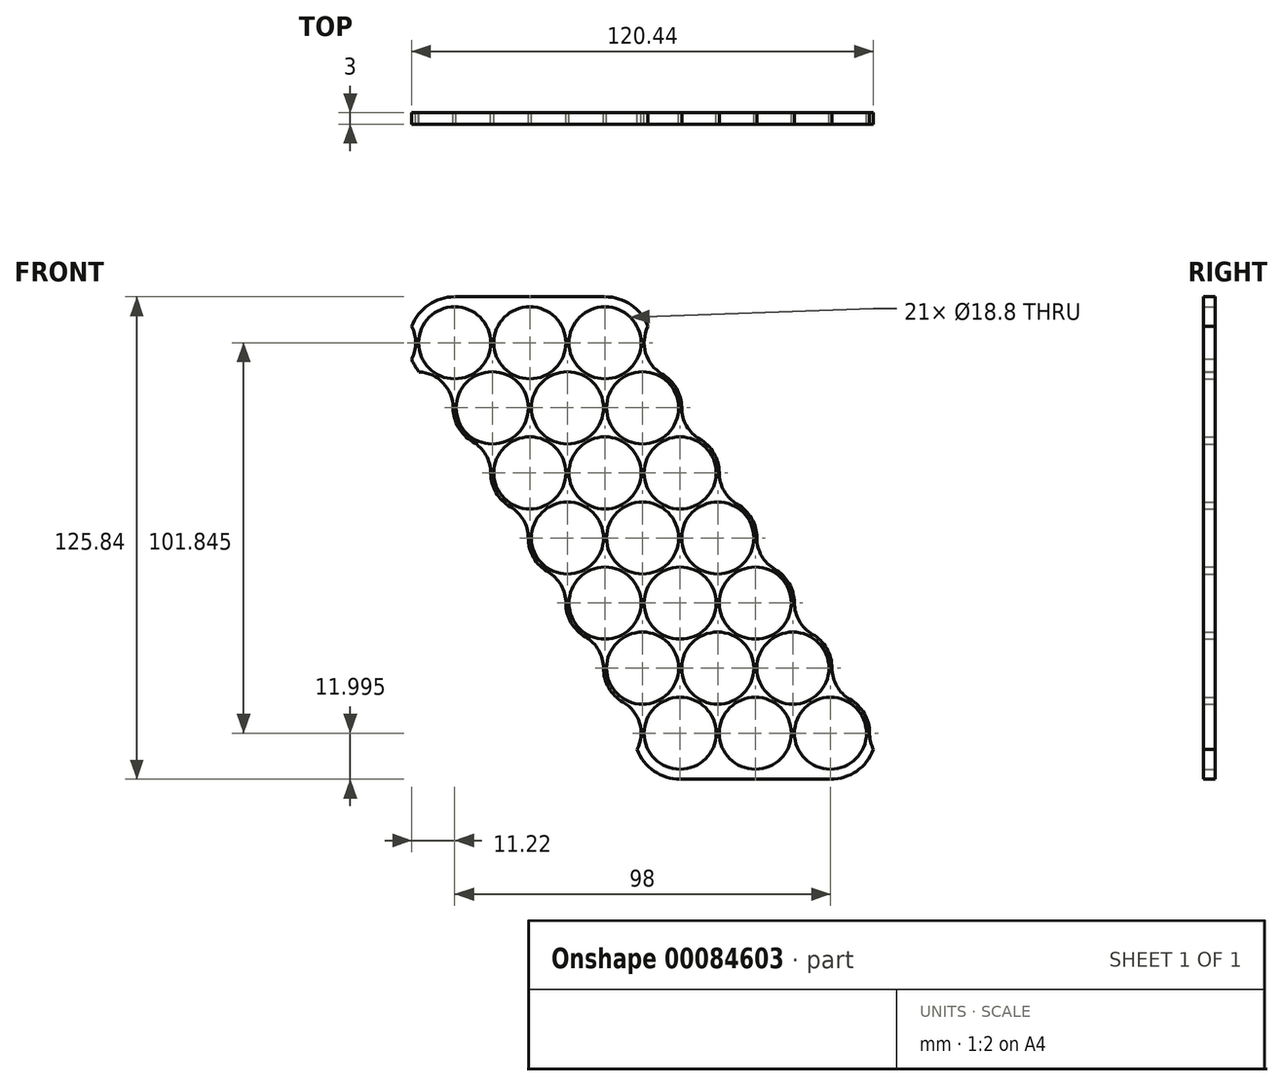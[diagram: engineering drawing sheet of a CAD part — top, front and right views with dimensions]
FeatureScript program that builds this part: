
annotation { "Feature Type Name" : "Feature", "Feature Type Description" : "" }
export const myFeature = defineFeature(function(context is Context, id is Id, definition is map)
    precondition{}
    {
        {
            var Q0;
            Q0=qCreatedBy(makeId("Front.planeOp"),FACE);
            var sketch = newSketch(context, id + "F0", { "sketchPlane" : qUnion([Q0]) });
            skLineSegment(sketch, "E0", {"start": v(0, 0) * mm, "end": v(43.4, -75.16) * mm, "construction": true});
            skCircle(sketch, "E1", {"center": v(0, 0) * mm, "radius": 9.4 * mm});
            skCircle(sketch, "E2.1.0.0", {"center": v(19.6, 0) * mm, "radius": 9.4 * mm});
            skCircle(sketch, "E2.2.0.0", {"center": v(39.2, 0) * mm, "radius": 9.4 * mm});
            skLineSegment(sketch, "E2.direction1", {"start": v(0, 0) * mm, "end": v(19.6, 0) * mm, "construction": true});
            skCircle(sketch, "E3.1.0.0", {"center": v(9.8, -16.97) * mm, "radius": 9.4 * mm});
            skCircle(sketch, "E3.2.0.0", {"center": v(19.6, -33.95) * mm, "radius": 9.4 * mm});
            skCircle(sketch, "E3.3.0.0", {"center": v(29.4, -50.92) * mm, "radius": 9.4 * mm});
            skCircle(sketch, "E3.4.0.0", {"center": v(39.2, -67.9) * mm, "radius": 9.4 * mm});
            skCircle(sketch, "E3.5.0.0", {"center": v(49, -84.87) * mm, "radius": 9.4 * mm});
            skCircle(sketch, "E3.6.0.0", {"center": v(58.8, -101.84) * mm, "radius": 9.4 * mm});
            skLineSegment(sketch, "E3.direction1", {"start": v(0, 0) * mm, "end": v(9.8, -16.97) * mm, "construction": true});
            skCircle(sketch, "E4.1.0.0", {"center": v(29.4, -16.97) * mm, "radius": 9.4 * mm});
            skCircle(sketch, "E4.1.0.1", {"center": v(39.2, -33.95) * mm, "radius": 9.4 * mm});
            skCircle(sketch, "E4.1.0.2", {"center": v(49, -50.92) * mm, "radius": 9.4 * mm});
            skCircle(sketch, "E4.1.0.3", {"center": v(58.8, -67.9) * mm, "radius": 9.4 * mm});
            skCircle(sketch, "E4.1.0.4", {"center": v(68.6, -84.87) * mm, "radius": 9.4 * mm});
            skCircle(sketch, "E4.1.0.5", {"center": v(78.4, -101.84) * mm, "radius": 9.4 * mm});
            skArc(sketch, "E4.2.0.0", {"start": v(44.3, -8.83) * mm, "mid": v(40.86, -21.67) * mm, "end": v(53.7, -25.11) * mm});
            skCircle(sketch, "E4.2.0.1", {"center": v(58.8, -33.95) * mm, "radius": 9.4 * mm});
            skCircle(sketch, "E4.2.0.2", {"center": v(68.6, -50.92) * mm, "radius": 9.4 * mm});
            skCircle(sketch, "E4.2.0.3", {"center": v(78.4, -67.9) * mm, "radius": 9.4 * mm});
            skCircle(sketch, "E4.2.0.4", {"center": v(88.2, -84.87) * mm, "radius": 9.4 * mm});
            skCircle(sketch, "E4.2.0.5", {"center": v(98, -101.84) * mm, "radius": 9.4 * mm});
            skLineSegment(sketch, "E4.direction1", {"start": v(9.8, -16.97) * mm, "end": v(29.4, -16.97) * mm, "construction": true});
            skLineSegment(sketch, "E5", {"start": v(58.8, -101.84) * mm, "end": v(0, 0) * mm, "construction": true});
            skArc(sketch, "E6", {"start": v(-0.4, -16.97) * mm, "mid": v(0.97, -22.07) * mm, "end": v(4.7, -25.8) * mm});
            skArc(sketch, "E7", {"start": v(9.4, -33.95) * mm, "mid": v(10.77, -39.05) * mm, "end": v(14.5, -42.78) * mm});
            skArc(sketch, "E8", {"start": v(19.2, -50.92) * mm, "mid": v(20.57, -56.02) * mm, "end": v(24.3, -59.76) * mm});
            skArc(sketch, "E9", {"start": v(29, -67.9) * mm, "mid": v(30.37, -73) * mm, "end": v(34.1, -76.73) * mm});
            skArc(sketch, "E10", {"start": v(38.8, -84.87) * mm, "mid": v(40.17, -89.97) * mm, "end": v(43.9, -93.7) * mm});
            skArc(sketch, "E11", {"start": v(88.6, -67.9) * mm, "mid": v(87.23, -62.8) * mm, "end": v(83.5, -59.06) * mm});
            skArc(sketch, "E12", {"start": v(78.8, -50.92) * mm, "mid": v(77.43, -45.82) * mm, "end": v(73.7, -42.09) * mm});
            skArc(sketch, "E13", {"start": v(59.2, -16.97) * mm, "mid": v(57.83, -11.87) * mm, "end": v(54.1, -8.14) * mm});
            skArc(sketch, "E14", {"start": v(44.3, -8.83) * mm, "mid": v(57.14, -12.27) * mm, "end": v(53.7, -25.11) * mm});
            skArc(sketch, "E15.trimOffspring", {"start": v(69, -33.95) * mm, "mid": v(67.63, -28.85) * mm, "end": v(63.9, -25.11) * mm});
            skArc(sketch, "E16.trimOffspring", {"start": v(98.4, -84.87) * mm, "mid": v(97.03, -79.77) * mm, "end": v(93.3, -76.04) * mm});
            skArc(sketch, "E17", {"start": v(49.4, 0) * mm, "mid": v(50.66, -4.7) * mm, "end": v(54.1, -8.14) * mm});
            skArc(sketch, "E18", {"start": v(59.2, -16.97) * mm, "mid": v(60.46, -21.67) * mm, "end": v(63.9, -25.11) * mm});
            skArc(sketch, "E19", {"start": v(69, -33.95) * mm, "mid": v(70.26, -38.65) * mm, "end": v(73.7, -42.09) * mm});
            skArc(sketch, "E20", {"start": v(78.8, -50.92) * mm, "mid": v(80.06, -55.62) * mm, "end": v(83.5, -59.06) * mm});
            skArc(sketch, "E21", {"start": v(88.6, -67.9) * mm, "mid": v(89.86, -72.6) * mm, "end": v(93.3, -76.04) * mm});
            skArc(sketch, "E22", {"start": v(98.4, -84.87) * mm, "mid": v(99.66, -89.57) * mm, "end": v(103.1, -93.01) * mm});
            skPoint(sketch, "E23.center.orphan", {"position": v(117.6, -101.84) * mm});
            skArc(sketch, "E24", {"start": v(-0.4, -16.97) * mm, "mid": v(-1.66, -12.27) * mm, "end": v(-5.1, -8.83) * mm});
            skArc(sketch, "E25", {"start": v(9.4, -33.95) * mm, "mid": v(8.14, -29.25) * mm, "end": v(4.7, -25.8) * mm});
            skArc(sketch, "E26", {"start": v(19.2, -50.92) * mm, "mid": v(17.94, -46.22) * mm, "end": v(14.5, -42.78) * mm});
            skArc(sketch, "E27", {"start": v(29, -67.9) * mm, "mid": v(27.74, -63.2) * mm, "end": v(24.3, -59.76) * mm});
            skArc(sketch, "E28", {"start": v(38.8, -84.87) * mm, "mid": v(37.54, -80.17) * mm, "end": v(34.1, -76.73) * mm});
            skArc(sketch, "E29", {"start": v(48.6, -101.84) * mm, "mid": v(47.34, -97.14) * mm, "end": v(43.9, -93.7) * mm});
            skPoint(sketch, "E30.centerSnap0", {"position": v(9.8, 0) * mm});
            skPoint(sketch, "E31.orphan", {"position": v(29.4, 2.83) * mm});
            skPoint(sketch, "E32.orphan", {"position": v(68.6, -104.67) * mm});
            skPoint(sketch, "E33.orphan", {"position": v(88.2, -104.67) * mm});
            skArc(sketch, "E34", {"start": v(0, 12) * mm, "mid": v(-6.82, 9.88) * mm, "end": v(-11.22, 4.26) * mm});
            skArc(sketch, "E35", {"start": v(50.42, 4.26) * mm, "mid": v(49.79, -2.68) * mm, "end": v(54.1, -8.14) * mm});
            skLineSegment(sketch, "E36", {"start": v(0, 12) * mm, "end": v(39.2, 12) * mm});
            skArc(sketch, "E37", {"start": v(-0.4, -16.97) * mm, "mid": v(-2.98, -10.5) * mm, "end": v(-9.3, -7.59) * mm});
            skArc(sketch, "E38.trimOffspring", {"start": v(50.42, 4.26) * mm, "mid": v(46.02, 9.88) * mm, "end": v(39.2, 12) * mm});
            skPoint(sketch, "E39.center.orphan", {"position": v(29.4, 16.97) * mm});
            skPoint(sketch, "E30.center.orphan", {"position": v(9.8, 16.97) * mm});
            skArc(sketch, "E40.trimOffspring", {"start": v(-1.92, -11.84) * mm, "mid": v(0, -12) * mm, "end": v(1.92, -11.84) * mm});
            skArc(sketch, "E41", {"start": v(-11.22, -4.26) * mm, "mid": v(-10.2, 0) * mm, "end": v(-11.22, 4.26) * mm});
            skArc(sketch, "E42.trimOffspring", {"start": v(-11.22, -4.26) * mm, "mid": v(-10.4, -6) * mm, "end": v(-9.3, -7.59) * mm});
            skArc(sketch, "E43", {"start": v(98, -113.84) * mm, "mid": v(104.82, -111.72) * mm, "end": v(109.22, -106.1) * mm});
            skArc(sketch, "E44", {"start": v(47.58, -106.1) * mm, "mid": v(51.98, -111.72) * mm, "end": v(58.8, -113.84) * mm});
            skArc(sketch, "E45", {"start": v(47.58, -106.1) * mm, "mid": v(48.21, -99.17) * mm, "end": v(43.9, -93.7) * mm});
            skArc(sketch, "E46.trimOffspring", {"start": v(60.72, -90) * mm, "mid": v(58.8, -89.84) * mm, "end": v(56.88, -90) * mm});
            skLineSegment(sketch, "E47", {"start": v(58.8, -113.84) * mm, "end": v(98, -113.84) * mm});
            skPoint(sketch, "E48.center.orphan", {"position": v(68.6, -118.82) * mm});
            skPoint(sketch, "E49.center.orphan", {"position": v(88.2, -118.82) * mm});
            skArc(sketch, "E50", {"start": v(108.2, -101.84) * mm, "mid": v(108.46, -104.03) * mm, "end": v(109.22, -106.1) * mm});
            skArc(sketch, "E51.trimOffspring", {"start": v(108.2, -101.84) * mm, "mid": v(106.83, -96.74) * mm, "end": v(103.1, -93.01) * mm});
            skArc(sketch, "E52", {"start": v(108.2, -101.84) * mm, "mid": v(108.46, -104.03) * mm, "end": v(109.22, -106.1) * mm, "construction": true});
            skArc(sketch, "E53", {"start": v(98.4, -84.87) * mm, "mid": v(99.66, -89.57) * mm, "end": v(103.1, -93.01) * mm, "construction": true});
            skArc(sketch, "E54.trimOffspring", {"start": v(98, -113.84) * mm, "mid": v(104.82, -111.72) * mm, "end": v(109.22, -106.1) * mm, "construction": true});
            skSolve(sketch);
        }
        {
            var Q0;
            Q0=makeQuery(id+"F0.imprint","IMPRINT",FACE,{"disambiguationData":[TD([[makeQuery(id+"F0.imprint","IMPRINT",EDGE,{"derivedFrom":sQuery(id+"F0.wireOp",EDGE,"E1")}),-1.0]])]});
            extrude(context, id + "F1", {"entities" : qUnion([Q0]), "depth" : 3 * mm});
        }
    });
